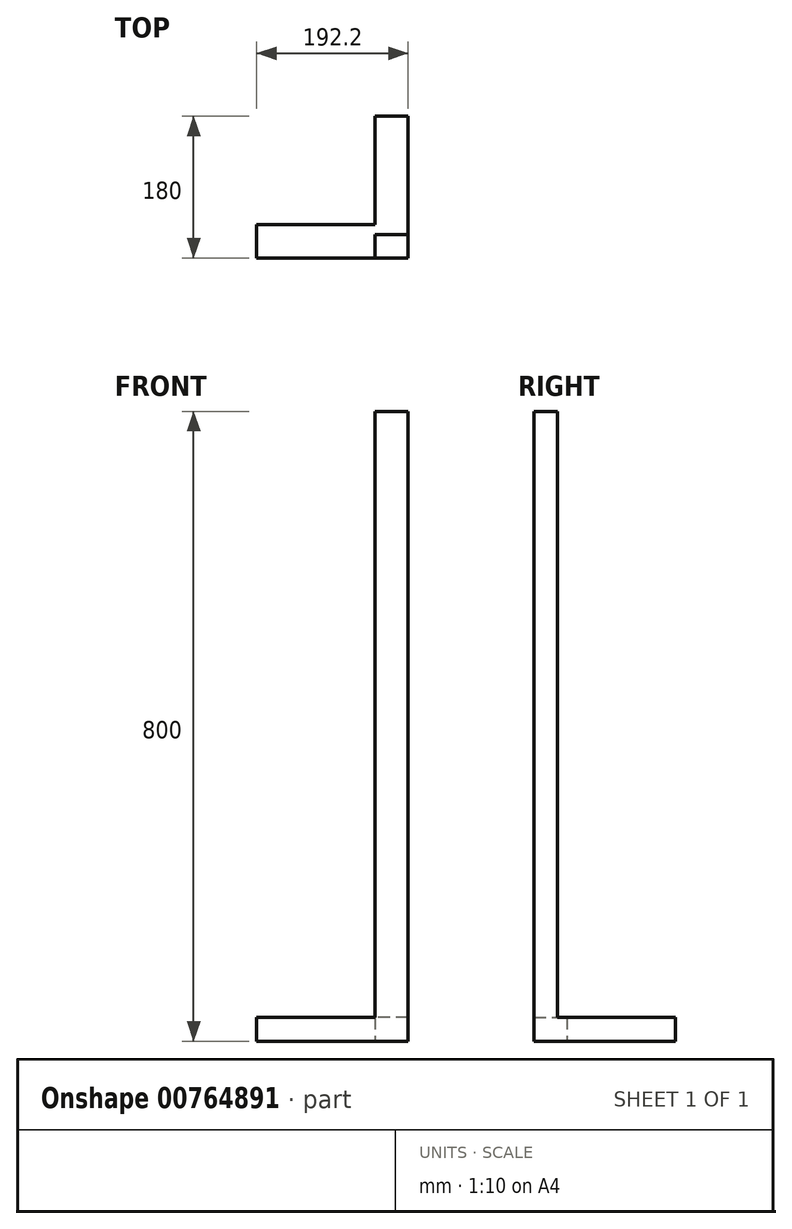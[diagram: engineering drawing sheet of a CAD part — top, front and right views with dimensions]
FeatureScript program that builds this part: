
annotation { "Feature Type Name" : "Feature", "Feature Type Description" : "" }
export const myFeature = defineFeature(function(context is Context, id is Id, definition is map)
    precondition{}
    {
        {
            var Q0;
            Q0=qCreatedBy(makeId("Top.planeOp"),FACE);
            var sketch = newSketch(context, id + "F0", { "sketchPlane" : qUnion([Q0])});
            skLineSegment(sketch, "E0.bottom", {"start": v(21.1, -15) * mm, "end": v(-21.1, -15) * mm});
            skLineSegment(sketch, "E0.top", {"start": v(21.1, 15) * mm, "end": v(-21.1, 15) * mm});
            skLineSegment(sketch, "E0.left", {"start": v(21.1, -15) * mm, "end": v(21.1, 15) * mm});
            skLineSegment(sketch, "E0.right", {"start": v(-21.1, -15) * mm, "end": v(-21.1, 15) * mm});
            skPoint(sketch, "E0.middle", {"position": v(0, 0) * mm});
            skLineSegment(sketch, "E1", {"start": v(21.1, 15) * mm, "end": v(21.1, 165) * mm});
            skLineSegment(sketch, "E2", {"start": v(21.1, 165) * mm, "end": v(-21.1, 165) * mm});
            skLineSegment(sketch, "E3", {"start": v(-21.1, 165) * mm, "end": v(-21.1, 15) * mm});
            skLineSegment(sketch, "E4", {"start": v(-21.1, -15) * mm, "end": v(-171.1, -15) * mm});
            skLineSegment(sketch, "E5", {"start": v(-171.1, -15) * mm, "end": v(-171.1, 27.2) * mm});
            skLineSegment(sketch, "E6", {"start": v(-171.1, 27.2) * mm, "end": v(-21.1, 27.2) * mm});
            skSolve(sketch);
        }
        {
            var Q0;
            Q0=makeQuery(id+"F0.imprint","IMPRINT",FACE,{"disambiguationData":[TD([[makeQuery(id+"F0.imprint","IMPRINT",EDGE,{"derivedFrom":sQuery(id+"F0.wireOp",EDGE,"E0.bottom")}),-1.0]])]});
            extrude(context, id + "F1", {"entities" : qUnion([Q0]), "depth" : 800 * mm, "offsetDistance" : 25 * mm});
        }
        {
            var Q0;
            {var subQ1=sQuery(id+"F0.wireOp",EDGE,"E0.right");Q0=makeQuery(id+"F0.imprint","IMPRINT",FACE,{"disambiguationData":[TD([[makeQuery(id+"F0.imprint","IMPRINT",EDGE,{"derivedFrom":subQ1}),1.0]])]});}
            var Q1;
            {var subQ3=sQuery(id+"F0.wireOp",EDGE,"E0.top");Q1=makeQuery(id+"F0.imprint","IMPRINT",FACE,{"disambiguationData":[TD([[makeQuery(id+"F0.imprint","IMPRINT",EDGE,{"derivedFrom":subQ3}),-1.0]])]});}
            extrude(context, id + "F2", {"entities" : qUnion([Q0, Q1]), "operationType" : NewBodyOperationType.ADD, "depth" : 30 * mm, "offsetDistance" : 25 * mm});
        }
    });
